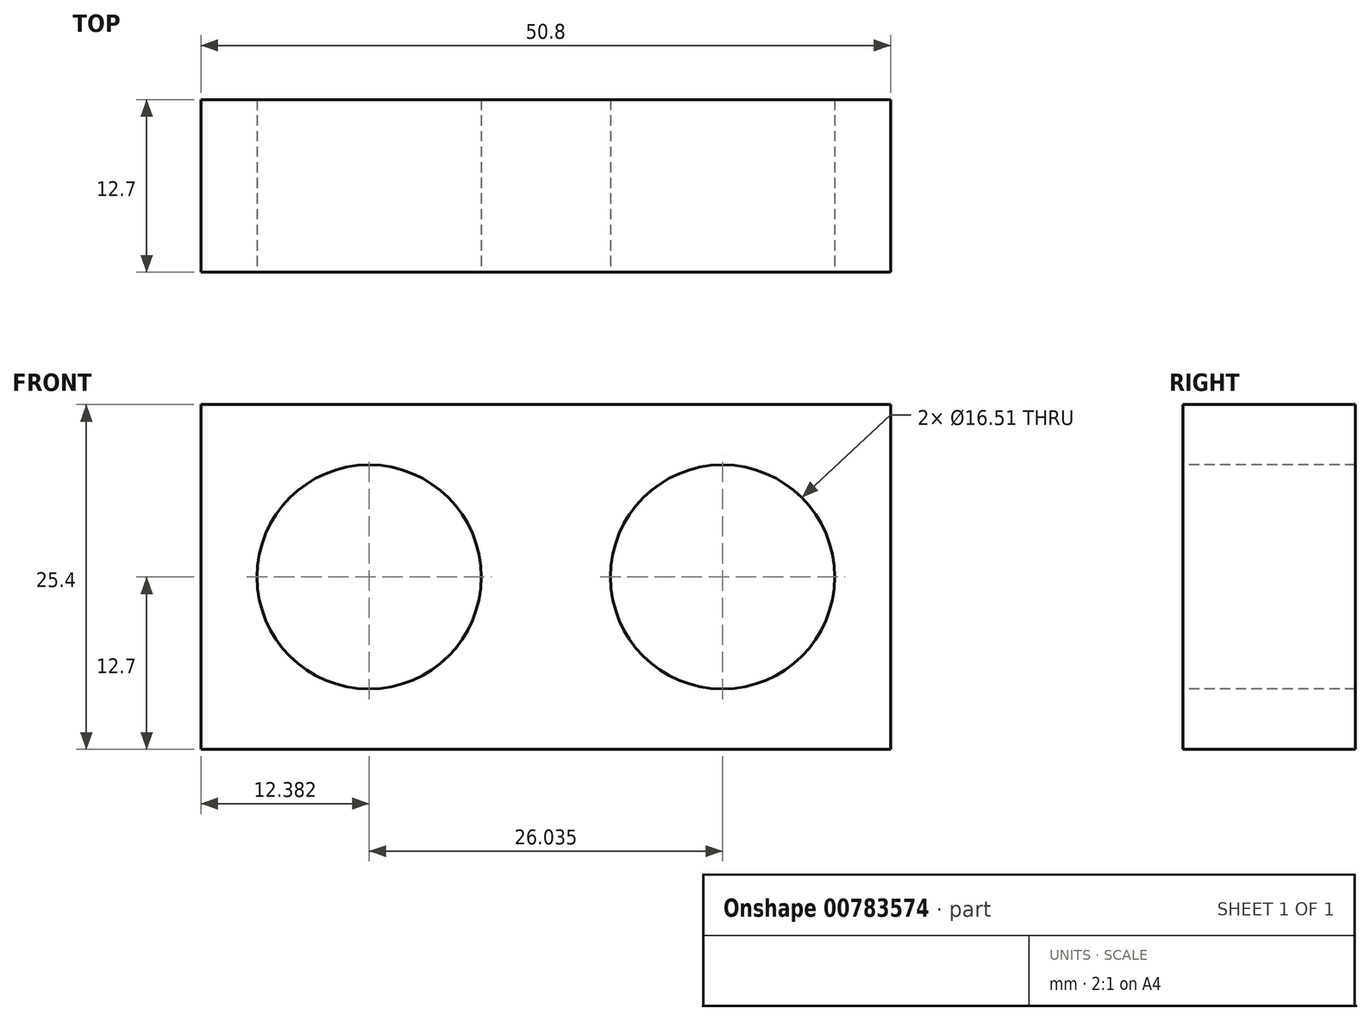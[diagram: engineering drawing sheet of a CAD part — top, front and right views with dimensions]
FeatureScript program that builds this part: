
annotation { "Feature Type Name" : "Feature", "Feature Type Description" : "" }
export const myFeature = defineFeature(function(context is Context, id is Id, definition is map)
    precondition{}
    {
        {
            var Q0;
            Q0=qCreatedBy(makeId("Front.planeOp"),FACE);
            var sketch = newSketch(context, id + "F0", { "sketchPlane" : qUnion([Q0])});
            skLineSegment(sketch, "E0.bottom", {"start": v(-25.4, 25.4) * mm, "end": v(25.4, 25.4) * mm});
            skLineSegment(sketch, "E0.top", {"start": v(-25.4, -25.4) * mm, "end": v(25.4, -25.4) * mm});
            skLineSegment(sketch, "E0.left", {"start": v(-25.4, 25.4) * mm, "end": v(-25.4, -25.4) * mm});
            skLineSegment(sketch, "E0.right", {"start": v(25.4, 25.4) * mm, "end": v(25.4, -25.4) * mm});
            skPoint(sketch, "E1", {"position": v(0, 0) * mm});
            skPoint(sketch, "E1.positionSnap0", {"position": v(-25.4, 0) * mm});
            skPoint(sketch, "E1.positionSnap1", {"position": v(0, 25.4) * mm});
            skSolve(sketch);
        }
        {
            var Q0;
            Q0=makeQuery(id+"F0.imprint","IMPRINT",FACE,{"disambiguationData":[TD([[makeQuery(id+"F0.imprint","IMPRINT",EDGE,{"derivedFrom":sQuery(id+"F0.wireOp",EDGE,"E0.bottom")}),-1.0]])]});
            extrude(context, id + "F1", {"entities" : qUnion([Q0]), "depth" : 25.4 * mm, "offsetDistance" : 25.4 * mm});
        }
        {
            var Q0;
            Q0=makeQuery(id+"F1.opExtrude","CAP_FACE",FACE,{"disambiguationData":[OSD([sQuery(id+"F0.wireOp",EDGE,"E0.bottom"),sQuery(id+"F0.wireOp",EDGE,"E0.top"),sQuery(id+"F0.wireOp",EDGE,"E0.left"),sQuery(id+"F0.wireOp",EDGE,"E0.right")])],"isStart":false});
            var sketch = newSketch(context, id + "F2", { "sketchPlane" : qUnion([Q0])});
            skLineSegment(sketch, "E2.bottom", {"start": v(-24.77, 11.11) * mm, "end": v(24.77, 11.11) * mm});
            skLineSegment(sketch, "E2.top", {"start": v(-24.77, -11.11) * mm, "end": v(24.77, -11.11) * mm});
            skLineSegment(sketch, "E2.left", {"start": v(-24.77, 11.11) * mm, "end": v(-24.77, -11.11) * mm});
            skLineSegment(sketch, "E2.right", {"start": v(24.77, 11.11) * mm, "end": v(24.77, -11.11) * mm});
            skPoint(sketch, "E3", {"position": v(0, 0) * mm});
            skPoint(sketch, "E3.positionSnap0", {"position": v(-24.77, 0) * mm});
            skPoint(sketch, "E3.positionSnap1", {"position": v(0, 11.11) * mm});
            skCircle(sketch, "E4", {"center": v(-13.02, 0) * mm, "radius": 8.26 * mm});
            skCircle(sketch, "E5", {"center": v(13.02, 0) * mm, "radius": 8.26 * mm});
            skLineSegment(sketch, "E6", {"start": v(13.02, 0) * mm, "end": v(-13.02, 0) * mm});
            skSolve(sketch);
        }
        {
            var Q0;
            Q0=makeQuery(id+"F2.imprint","IMPRINT",FACE,{"disambiguationData":[TD([[makeQuery(id+"F2.imprint","IMPRINT",EDGE,{"derivedFrom":sQuery(id+"F2.wireOp",EDGE,"E4")}),1.0]])]});
            var Q1;
            Q1=makeQuery(id+"F2.imprint","IMPRINT",FACE,{"disambiguationData":[TD([[makeQuery(id+"F2.imprint","IMPRINT",EDGE,{"derivedFrom":sQuery(id+"F2.wireOp",EDGE,"E5")}),1.0]])]});
            extrude(context, id + "F3", {"entities" : qUnion([Q0, Q1]), "operationType" : NewBodyOperationType.REMOVE, "oppositeDirection" : true, "depth" : 25.4 * mm, "offsetDistance" : 25.4 * mm});
        }
        {
            var Q0;
            Q0=makeQuery(id+"F1.opExtrude","CAP_FACE",FACE,{"disambiguationData":[OSD([sQuery(id+"F0.wireOp",EDGE,"E0.bottom"),sQuery(id+"F0.wireOp",EDGE,"E0.top"),sQuery(id+"F0.wireOp",EDGE,"E0.left"),sQuery(id+"F0.wireOp",EDGE,"E0.right")])],"isStart":false});
            extrude(context, id + "F4", {"entities" : qUnion([Q0]), "operationType" : NewBodyOperationType.REMOVE, "oppositeDirection" : true, "depth" : 12.7 * mm, "offsetDistance" : 25.4 * mm});
        }
        {
            var Q0;
            Q0=makeQuery(id+"F1.opExtrude","SWEPT_FACE",FACE,{"disambiguationData":[OSD([sQuery(id+"F0.wireOp",EDGE,"E0.bottom")])]});
            extrude(context, id + "F5", {"entities" : qUnion([Q0]), "operationType" : NewBodyOperationType.REMOVE, "oppositeDirection" : true, "depth" : 12.7 * mm, "offsetDistance" : 25.4 * mm});
        }
        {
            var Q0;
            Q0=makeQuery(id+"F1.opExtrude","SWEPT_FACE",FACE,{"disambiguationData":[OSD([sQuery(id+"F0.wireOp",EDGE,"E0.top")])]});
            extrude(context, id + "F6", {"entities" : qUnion([Q0]), "operationType" : NewBodyOperationType.REMOVE, "oppositeDirection" : true, "depth" : 12.7 * mm, "offsetDistance" : 25.4 * mm});
        }
    });
